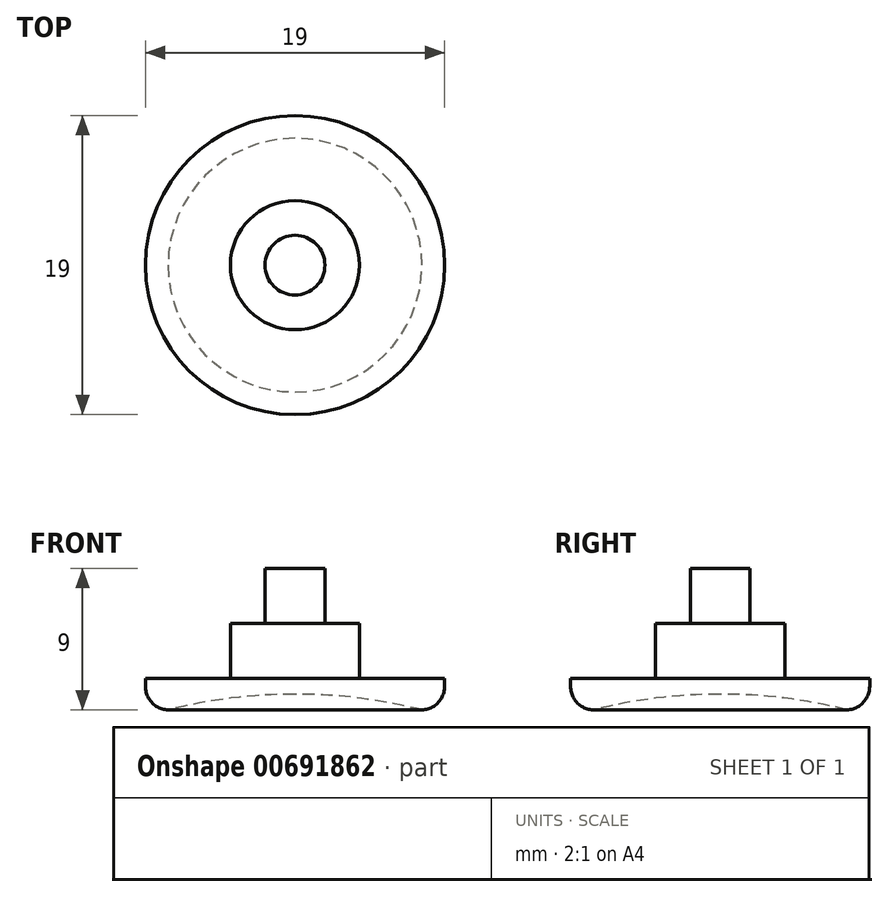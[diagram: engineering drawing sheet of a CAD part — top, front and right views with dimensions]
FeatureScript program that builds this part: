
annotation { "Feature Type Name" : "Feature", "Feature Type Description" : "" }
export const myFeature = defineFeature(function(context is Context, id is Id, definition is map)
    precondition{}
    {
        {
            var Q0;
            Q0=qCreatedBy(makeId("Top.planeOp"),FACE);
            var sketch = newSketch(context, id + "F0", { "sketchPlane" : qUnion([Q0])});
            skCircle(sketch, "E0", {"center": v(0, 0) * mm, "radius": 9.5 * mm});
            skCircle(sketch, "E1", {"center": v(0, 0) * mm, "radius": 4.1 * mm});
            skCircle(sketch, "E2", {"center": v(0, 0) * mm, "radius": 1.9 * mm});
            skSolve(sketch);
        }
        {
            var Q0;
            Q0=makeQuery(id+"F0.imprint","IMPRINT",FACE,{"disambiguationData":[TD([[makeQuery(id+"F0.imprint","IMPRINT",EDGE,{"derivedFrom":sQuery(id+"F0.wireOp",EDGE,"E0")}),1.0]])]});
            var Q1;
            Q1=makeQuery(id+"F0.imprint","IMPRINT",FACE,{"disambiguationData":[TD([[makeQuery(id+"F0.imprint","IMPRINT",EDGE,{"derivedFrom":sQuery(id+"F0.wireOp",EDGE,"E1")}),1.0]])]});
            var Q2;
            Q2=makeQuery(id+"F0.imprint","IMPRINT",FACE,{"disambiguationData":[TD([[makeQuery(id+"F0.imprint","IMPRINT",EDGE,{"derivedFrom":sQuery(id+"F0.wireOp",EDGE,"E2")}),1.0]])]});
            var Q3;
            Q3=qSketchRegion(id+"F2",true);
            extrude(context, id + "F1", {"entities" : qUnion([Q0, Q1, Q2, Q3]), "depth" : 2 * mm, "offsetDistance" : 25 * mm});
        }
        {
            var Q0;
            Q0=qCreatedBy(makeId("Top.planeOp"),FACE);
            var sketch = newSketch(context, id + "F2", { "sketchPlane" : qUnion([Q0])});
            skCircle(sketch, "E3", {"center": v(0, 0) * mm, "radius": 1.9 * mm});
            skCircle(sketch, "E4", {"center": v(0, 0) * mm, "radius": 4.1 * mm});
            skSolve(sketch);
        }
        {
            var Q0;
            Q0=qSketchRegion(id+"F2",true);
            extrude(context, id + "F3", {"entities" : qUnion([Q0]), "operationType" : NewBodyOperationType.ADD, "depth" : 5.5 * mm, "offsetDistance" : 25 * mm});
        }
        {
            var Q0;
            Q0=makeQuery(id+"F1.opExtrude","CAP_EDGE",EDGE,{"disambiguationData":[OSD([sQuery(id+"F0.wireOp",EDGE,"E0")])],"isStart":true});
            fillet(context, id + "F4", {"entities" : qUnion([Q0]), "radius" : 1.5 * mm, "tangentPropagation" : true, "allowEdgeOverflow" : false});
        }
        {
            var Q0;
            Q0=qCreatedBy(makeId("Front.planeOp"),FACE);
            var sketch = newSketch(context, id + "F5", { "sketchPlane" : qUnion([Q0])});
            skLineSegment(sketch, "E5", {"start": v(0, 10.26) * mm, "end": v(0, -73.29) * mm, "construction": true});
            skLineSegment(sketch, "E6", {"start": v(10.25, 0) * mm, "end": v(10.25, 1) * mm, "construction": true});
            skLineSegment(sketch, "E7", {"start": v(10.25, 1) * mm, "end": v(-10.7, 1) * mm, "construction": true});
            skArc(sketch, "E8", {"start": v(33, -32.5) * mm, "mid": v(23.51, -8.84) * mm, "end": v(0, 1) * mm});
            skPoint(sketch, "E9", {"position": v(0, 1) * mm});
            skPoint(sketch, "E10", {"position": v(0, -65) * mm});
            skArc(sketch, "E11", {"start": v(33, -32.5) * mm, "mid": v(23.16, -9.49) * mm, "end": v(0, 0) * mm});
            skPoint(sketch, "E12", {"position": v(0, -66) * mm});
            skPoint(sketch, "E13", {"position": v(0, 0) * mm});
            skLineSegment(sketch, "E14", {"start": v(0, 1) * mm, "end": v(0, 0) * mm});
            skSolve(sketch);
        }
        {
            var Q0;
            Q0=makeQuery(id+"F5.imprint","IMPRINT",FACE,{"disambiguationData":[TD([[makeQuery(id+"F5.imprint","IMPRINT",EDGE,{"derivedFrom":sQuery(id+"F5.wireOp",EDGE,"E8")}),1.0]])]});
            var Q1;
            Q1=sQuery(id+"F5.wireOp",EDGE,"E5");
            revolve(context, id + "F6", {"operationType" : NewBodyOperationType.REMOVE, "entities" : qUnion([Q0]), "axis" : qUnion([Q1]), "revolveType" : RevolveType.FULL});
        }
        {
            var Q0;
            Q0=makeQuery(id+"F3.boolean.opBoolean","SPLIT",FACE,{"disambiguationData":[TD([makeQuery(id+"F3.opExtrude","SWEPT_FACE",FACE,{"disambiguationData":[OSD([sQuery(id+"F2.wireOp",EDGE,"E3")])]})])],"derivedFrom":makeQuery(id+"F1.opExtrude","CAP_FACE",FACE,{"disambiguationData":[OSD([sQuery(id+"F0.wireOp",EDGE,"E0")])],"isStart":false})});
            extrude(context, id + "F7", {"entities" : qUnion([Q0]), "operationType" : NewBodyOperationType.ADD, "depth" : 7 * mm, "offsetDistance" : 25 * mm});
        }
    });
